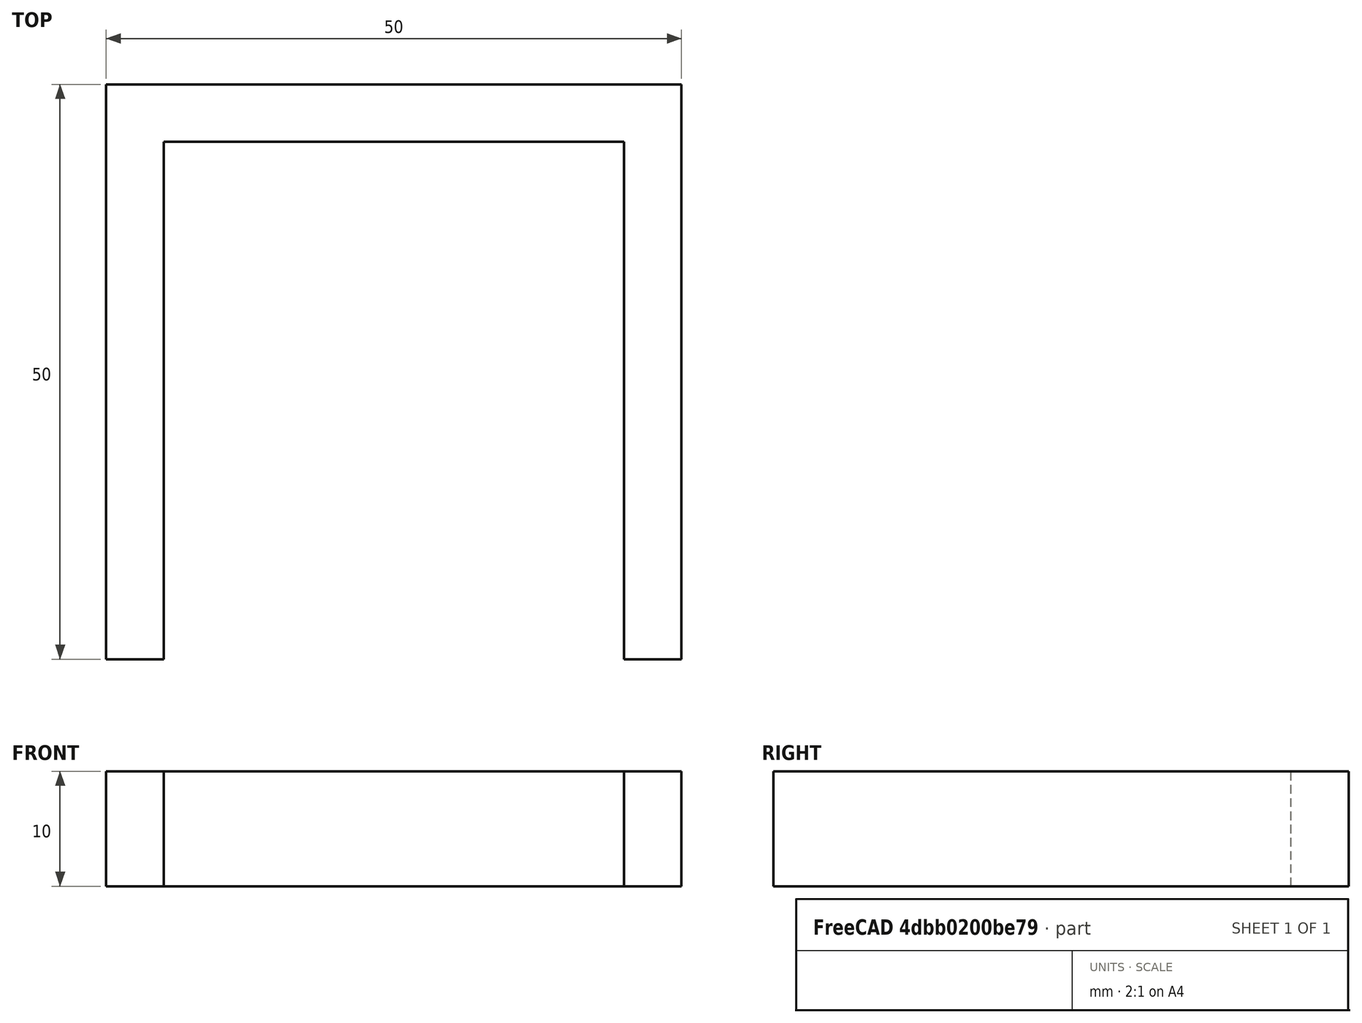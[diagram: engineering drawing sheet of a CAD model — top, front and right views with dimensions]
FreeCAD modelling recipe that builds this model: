
FCSTD DOCUMENT  (FreeCAD 2023.1231R38924 (Git))
Label: PCB_Spacer
License: All rights reserved
LicenseURL: https://en.wikipedia.org/wiki/All_rights_reserved
objects: Sketcher::SketchObject×1, PartDesign::Pad×1, PartDesign::Body×1
note: 6 computed .brp shape members not serialized (recipe doc carries the construction recipe); baked Part::Feature solids carry a one-line shape summary decoded from their .brp

FEATURE [Sketcher::SketchObject] Sketch
  ArcFitTolerance = 1e-06
  AttachmentSupport = -> [XY_Plane]
  ExternalBSplineMaxDegree = 5
  ExternalBSplineTolerance = 0.0001
  FullyConstrained = true
  InternalTolerance = 1e-06
  InvalidShape = false
  MakeInternals = false
  MapMode = 5
  Support = -> [XY_Plane]
  TreeRank = 11
  ValidateShape = false
  sketch-geometry (8):
    g0: LineSegment StartX=-25 StartY=0 StartZ=0 EndX=25 EndY=0 EndZ=0
    g1: LineSegment StartX=25 StartY=0 StartZ=0 EndX=25 EndY=-50 EndZ=0
    g2: LineSegment StartX=25 StartY=-50 StartZ=0 EndX=20 EndY=-50 EndZ=0
    g3: LineSegment StartX=20 StartY=-50 StartZ=0 EndX=20 EndY=-5 EndZ=0
    g4: LineSegment StartX=20 StartY=-5 StartZ=0 EndX=-20 EndY=-5 EndZ=0
    g5: LineSegment StartX=-20 StartY=-5 StartZ=0 EndX=-20 EndY=-50 EndZ=0
    g6: LineSegment StartX=-20 StartY=-50 StartZ=0 EndX=-25 EndY=-50 EndZ=0
    g7: LineSegment StartX=-25 StartY=-50 StartZ=0 EndX=-25 EndY=0 EndZ=0
  constraints (22):
    c: PointOnObject(g0,g-1)
    c: Coincident(g0,g1)
    c: Vertical(g1)
    c: Coincident(g1,g2)
    c: Coincident(g2,g3)
    c: Coincident(g3,g4)
    c: Coincident(g4,g5)
    c: Coincident(g5,g6)
    c: Coincident(g6,g7)
    c: Coincident(g7,g0)
    c: Symmetric(g0,g0,g-2)
    c: Symmetric(g4,g3,g-2)
    c: Horizontal(g6)
    c: Horizontal(g2)
    c: Vertical(g3)
    c: Vertical(g5)
    c: Vertical(g7)
    c: Equal(g5,g3)
    c: DistanceX(g2,g2) = 5
    c: DistanceY(g1,g1) = 50
    c: DistanceX(g0,g0) = 50
    c: DistanceY(g3,g0) = 5
FEATURE [PartDesign::Pad] Pad
  AddSubType = 0
  AlongSketchNormal = false
  AutoTaperInnerAngle = true
  CheckUpToFaceLimits = true
  ClaimChildren = false
  Direction = (0,0,1)
  Fit = 0
  FitJoin = 0
  InnerFit = 0
  InnerFitJoin = 0
  InvalidShape = false
  Length = 10
  Length2 = 10
  Linearize = true
  NewSolid = false
  Profile = -> Sketch
  ReferenceAxis = -> Sketch [N_Axis]
  Suppress = false
  TaperInnerAngle = 0
  TaperInnerAngleRev = 0
  TreeRank = 12
  Type = 0
  ValidateShape = true
  _ProfileBasedVersion = 1
FEATURE [PartDesign::Body] Body
  AutoGroupSolids = false
  ClaimAllChildren = false
  ExportMode = 0
  Group = -> [Sketch,Pad]
  InvalidShape = false
  Origin = -> Origin
  Tip = -> Pad
  TreeRank = 10
  ValidateShape = false
  _ExportChildren = -> [Pad]
  _GroupVersion = 1
